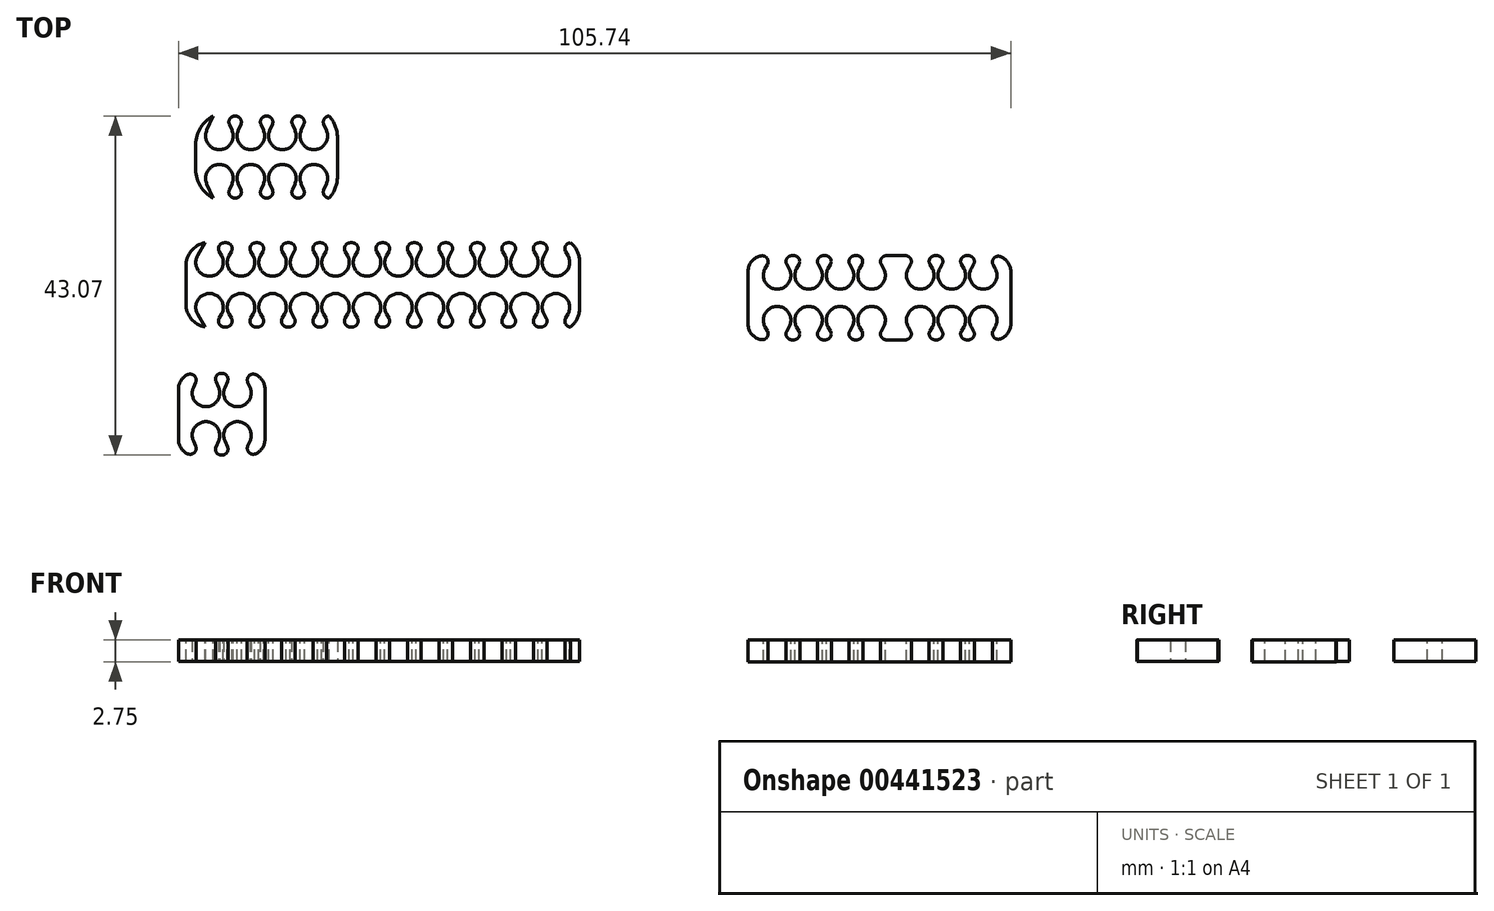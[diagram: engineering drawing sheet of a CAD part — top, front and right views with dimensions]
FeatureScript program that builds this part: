
annotation { "Feature Type Name" : "Feature", "Feature Type Description" : "" }
export const myFeature = defineFeature(function(context is Context, id is Id, definition is map)
    precondition{}
    {
        {
            var Q0;
            Q0=qCreatedBy(makeId("Top.planeOp"),FACE);
            var sketch = newSketch(context, id + "F0", { "sketchPlane" : qUnion([Q0])});
            skLineSegment(sketch, "E0.bottom", {"start": v(-25, 10.7) * mm, "end": v(25, 10.7) * mm});
            skLineSegment(sketch, "E0.top", {"start": v(-25, 0) * mm, "end": v(25, 0) * mm});
            skLineSegment(sketch, "E0.left", {"start": v(-25, 10.7) * mm, "end": v(-25, 0) * mm});
            skLineSegment(sketch, "E0.right", {"start": v(25, 10.7) * mm, "end": v(25, 0) * mm});
            skSolve(sketch);
        }
        {
            var Q0;
            Q0=makeQuery(id+"F0.imprint","IMPRINT",FACE,{"disambiguationData":[TD([[makeQuery(id+"F0.imprint","IMPRINT",EDGE,{"derivedFrom":sQuery(id+"F0.wireOp",EDGE,"E0.bottom")}),-1.0]])]});
            extrude(context, id + "F1", {"entities" : qUnion([Q0]), "depth" : 2.7 * mm});
        }
        {
            var Q0;
            Q0=makeQuery(id+"F1.opExtrude","CAP_FACE",FACE,{"disambiguationData":[OSD([sQuery(id+"F0.wireOp",EDGE,"E0.bottom"),sQuery(id+"F0.wireOp",EDGE,"E0.top"),sQuery(id+"F0.wireOp",EDGE,"E0.left"),sQuery(id+"F0.wireOp",EDGE,"E0.right")])],"isStart":false});
            var sketch = newSketch(context, id + "F2", { "sketchPlane" : qUnion([Q0])});
            skArc(sketch, "E1", {"start": v(-23.52, 9.07) * mm, "mid": v(-22, 6.45) * mm, "end": v(-20.48, 9.07) * mm});
            skArc(sketch, "E2", {"start": v(-19.52, 9.07) * mm, "mid": v(-18, 6.45) * mm, "end": v(-16.48, 9.07) * mm});
            skArc(sketch, "E3", {"start": v(-15.52, 9.07) * mm, "mid": v(-14, 6.45) * mm, "end": v(-12.48, 9.07) * mm});
            skArc(sketch, "E4", {"start": v(-11.52, 9.07) * mm, "mid": v(-10, 6.45) * mm, "end": v(-8.48, 9.07) * mm});
            skArc(sketch, "E5", {"start": v(-7.52, 9.07) * mm, "mid": v(-6, 6.45) * mm, "end": v(-4.48, 9.07) * mm});
            skArc(sketch, "E6", {"start": v(-3.52, 9.07) * mm, "mid": v(-2, 6.45) * mm, "end": v(-0.48, 9.07) * mm});
            skLineSegment(sketch, "E7", {"start": v(-19.52, 9.07) * mm, "end": v(-18.59, 10.7) * mm});
            skLineSegment(sketch, "E8", {"start": v(-16.48, 9.07) * mm, "end": v(-17.41, 10.7) * mm});
            skLineSegment(sketch, "E9", {"start": v(-15.52, 9.07) * mm, "end": v(-14.59, 10.7) * mm});
            skLineSegment(sketch, "E10", {"start": v(-12.48, 9.07) * mm, "end": v(-13.41, 10.7) * mm});
            skLineSegment(sketch, "E11", {"start": v(-11.52, 9.07) * mm, "end": v(-10.59, 10.7) * mm});
            skLineSegment(sketch, "E12", {"start": v(-8.48, 9.07) * mm, "end": v(-9.41, 10.7) * mm});
            skLineSegment(sketch, "E13", {"start": v(-7.52, 9.07) * mm, "end": v(-6.59, 10.7) * mm});
            skLineSegment(sketch, "E14", {"start": v(-4.48, 9.07) * mm, "end": v(-5.41, 10.7) * mm});
            skLineSegment(sketch, "E15", {"start": v(-0.48, 9.07) * mm, "end": v(-1.41, 10.7) * mm});
            skLineSegment(sketch, "E16", {"start": v(-23.52, 9.07) * mm, "end": v(-22.59, 10.7) * mm});
            skLineSegment(sketch, "E17", {"start": v(-18.59, 10.7) * mm, "end": v(-17.41, 10.7) * mm});
            skLineSegment(sketch, "E18", {"start": v(-14.59, 10.7) * mm, "end": v(-13.41, 10.7) * mm});
            skLineSegment(sketch, "E19", {"start": v(-10.59, 10.7) * mm, "end": v(-9.41, 10.7) * mm});
            skLineSegment(sketch, "E20", {"start": v(-6.59, 10.7) * mm, "end": v(-5.41, 10.7) * mm});
            skLineSegment(sketch, "E21", {"start": v(-2.59, 10.7) * mm, "end": v(-1.41, 10.7) * mm});
            skLineSegment(sketch, "E22", {"start": v(-25, 5.35) * mm, "end": v(25, 5.35) * mm});
            skLineSegment(sketch, "E23.MirrorCS", {"start": v(-15.52, 1.63) * mm, "end": v(-14.59, 0) * mm});
            skLineSegment(sketch, "E24.MirrorCS", {"start": v(-8.48, 1.63) * mm, "end": v(-9.41, 0) * mm});
            skLineSegment(sketch, "E25.MirrorCS", {"start": v(-7.52, 1.63) * mm, "end": v(-6.59, 0) * mm});
            skLineSegment(sketch, "E26.MirrorCS", {"start": v(-16.48, 1.63) * mm, "end": v(-17.41, 0) * mm});
            skLineSegment(sketch, "E27.MirrorCS", {"start": v(-4.48, 1.63) * mm, "end": v(-5.41, 0) * mm});
            skArc(sketch, "E28.MirrorCS", {"start": v(-23.52, 1.63) * mm, "mid": v(-22, 4.25) * mm, "end": v(-20.48, 1.63) * mm});
            skArc(sketch, "E29.MirrorCS", {"start": v(-3.52, 1.63) * mm, "mid": v(-2, 4.25) * mm, "end": v(-0.48, 1.63) * mm});
            skLineSegment(sketch, "E30.MirrorCS", {"start": v(-19.52, 1.63) * mm, "end": v(-18.59, 0) * mm});
            skArc(sketch, "E31.MirrorCS", {"start": v(-19.52, 1.63) * mm, "mid": v(-18, 4.25) * mm, "end": v(-16.48, 1.63) * mm});
            skArc(sketch, "E32.MirrorCS", {"start": v(-7.52, 1.63) * mm, "mid": v(-6, 4.25) * mm, "end": v(-4.48, 1.63) * mm});
            skArc(sketch, "E33.MirrorCS", {"start": v(-11.52, 1.63) * mm, "mid": v(-10, 4.25) * mm, "end": v(-8.48, 1.63) * mm});
            skArc(sketch, "E34.MirrorCS", {"start": v(-15.52, 1.63) * mm, "mid": v(-14, 4.25) * mm, "end": v(-12.48, 1.63) * mm});
            skLineSegment(sketch, "E35.MirrorCS", {"start": v(-23.52, 1.63) * mm, "end": v(-22.59, 0) * mm});
            skLineSegment(sketch, "E36.MirrorCS", {"start": v(-2.59, 0) * mm, "end": v(-1.41, 0) * mm});
            skLineSegment(sketch, "E37.MirrorCS", {"start": v(-6.59, 0) * mm, "end": v(-5.41, 0) * mm});
            skLineSegment(sketch, "E38.MirrorCS", {"start": v(-18.59, 0) * mm, "end": v(-17.41, 0) * mm});
            skLineSegment(sketch, "E39.MirrorCS", {"start": v(-11.52, 1.63) * mm, "end": v(-10.59, 0) * mm});
            skLineSegment(sketch, "E40.MirrorCS", {"start": v(-14.59, 0) * mm, "end": v(-13.41, 0) * mm});
            skLineSegment(sketch, "E41.MirrorCS", {"start": v(-10.59, 0) * mm, "end": v(-9.41, 0) * mm});
            skLineSegment(sketch, "E42.MirrorCS", {"start": v(-12.48, 1.63) * mm, "end": v(-13.41, 0) * mm});
            skLineSegment(sketch, "E43.MirrorCS", {"start": v(-0.48, 1.63) * mm, "end": v(-1.41, 0) * mm});
            skLineSegment(sketch, "E44", {"start": v(-3.52, 9.07) * mm, "end": v(-2.59, 10.7) * mm});
            skLineSegment(sketch, "E45", {"start": v(-3.52, 1.63) * mm, "end": v(-2.59, 0) * mm});
            skLineSegment(sketch, "E46", {"start": v(-20.48, 9.07) * mm, "end": v(-21.41, 10.7) * mm});
            skLineSegment(sketch, "E47", {"start": v(-21.41, 10.7) * mm, "end": v(-22.59, 10.7) * mm});
            skLineSegment(sketch, "E48", {"start": v(-20.48, 1.63) * mm, "end": v(-21.41, 0) * mm});
            skLineSegment(sketch, "E49", {"start": v(-21.41, 0) * mm, "end": v(-22.59, 0) * mm});
            skLineSegment(sketch, "E50.MirrorCS", {"start": v(6.59, 0) * mm, "end": v(5.41, 0) * mm});
            skLineSegment(sketch, "E51.MirrorCS", {"start": v(21.41, 0) * mm, "end": v(22.59, 0) * mm});
            skLineSegment(sketch, "E52.MirrorCS", {"start": v(10.59, 10.7) * mm, "end": v(9.41, 10.7) * mm});
            skLineSegment(sketch, "E53.MirrorCS", {"start": v(6.59, 10.7) * mm, "end": v(5.41, 10.7) * mm});
            skLineSegment(sketch, "E54.MirrorCS", {"start": v(21.41, 10.7) * mm, "end": v(22.59, 10.7) * mm});
            skLineSegment(sketch, "E55.MirrorCS", {"start": v(18.59, 10.7) * mm, "end": v(17.41, 10.7) * mm});
            skLineSegment(sketch, "E56.MirrorCS", {"start": v(2.59, 0) * mm, "end": v(1.41, 0) * mm});
            skLineSegment(sketch, "E57.MirrorCS", {"start": v(18.59, 0) * mm, "end": v(17.41, 0) * mm});
            skLineSegment(sketch, "E58.MirrorCS", {"start": v(2.59, 10.7) * mm, "end": v(1.41, 10.7) * mm});
            skLineSegment(sketch, "E59.MirrorCS", {"start": v(10.59, 0) * mm, "end": v(9.41, 0) * mm});
            skLineSegment(sketch, "E60.MirrorCS", {"start": v(14.59, 10.7) * mm, "end": v(13.41, 10.7) * mm});
            skLineSegment(sketch, "E61.MirrorCS", {"start": v(14.59, 0) * mm, "end": v(13.41, 0) * mm});
            skArc(sketch, "E62.MirrorCS", {"start": v(11.52, 9.07) * mm, "mid": v(10, 6.45) * mm, "end": v(8.48, 9.07) * mm});
            skLineSegment(sketch, "E63.MirrorCS", {"start": v(15.52, 1.63) * mm, "end": v(14.59, 0) * mm});
            skArc(sketch, "E64.MirrorCS", {"start": v(15.52, 1.63) * mm, "mid": v(14, 4.25) * mm, "end": v(12.48, 1.63) * mm});
            skLineSegment(sketch, "E65.MirrorCS", {"start": v(4.48, 1.63) * mm, "end": v(5.41, 0) * mm});
            skArc(sketch, "E66.MirrorCS", {"start": v(3.52, 1.63) * mm, "mid": v(2, 4.25) * mm, "end": v(0.48, 1.63) * mm});
            skArc(sketch, "E67.MirrorCS", {"start": v(3.52, 9.07) * mm, "mid": v(2, 6.45) * mm, "end": v(0.48, 9.07) * mm});
            skLineSegment(sketch, "E68.MirrorCS", {"start": v(15.52, 9.07) * mm, "end": v(14.59, 10.7) * mm});
            skLineSegment(sketch, "E69.MirrorCS", {"start": v(12.48, 9.07) * mm, "end": v(13.41, 10.7) * mm});
            skLineSegment(sketch, "E70.MirrorCS", {"start": v(16.48, 9.07) * mm, "end": v(17.41, 10.7) * mm});
            skLineSegment(sketch, "E71.MirrorCS", {"start": v(23.52, 9.07) * mm, "end": v(22.59, 10.7) * mm});
            skArc(sketch, "E72.MirrorCS", {"start": v(7.52, 9.07) * mm, "mid": v(6, 6.45) * mm, "end": v(4.48, 9.07) * mm});
            skLineSegment(sketch, "E73.MirrorCS", {"start": v(25, 5.35) * mm, "end": v(-25, 5.35) * mm});
            skLineSegment(sketch, "E74.MirrorCS", {"start": v(7.52, 1.63) * mm, "end": v(6.59, 0) * mm});
            skArc(sketch, "E75.MirrorCS", {"start": v(19.52, 9.07) * mm, "mid": v(18, 6.45) * mm, "end": v(16.48, 9.07) * mm});
            skLineSegment(sketch, "E76.MirrorCS", {"start": v(3.52, 1.63) * mm, "end": v(2.59, 0) * mm});
            skLineSegment(sketch, "E77.MirrorCS", {"start": v(19.52, 1.63) * mm, "end": v(18.59, 0) * mm});
            skLineSegment(sketch, "E78.MirrorCS", {"start": v(23.52, 1.63) * mm, "end": v(22.59, 0) * mm});
            skArc(sketch, "E79.MirrorCS", {"start": v(15.52, 9.07) * mm, "mid": v(14, 6.45) * mm, "end": v(12.48, 9.07) * mm});
            skArc(sketch, "E80.MirrorCS", {"start": v(11.52, 1.63) * mm, "mid": v(10, 4.25) * mm, "end": v(8.48, 1.63) * mm});
            skArc(sketch, "E81.MirrorCS", {"start": v(7.52, 1.63) * mm, "mid": v(6, 4.25) * mm, "end": v(4.48, 1.63) * mm});
            skLineSegment(sketch, "E82.MirrorCS", {"start": v(12.48, 1.63) * mm, "end": v(13.41, 0) * mm});
            skLineSegment(sketch, "E83.MirrorCS", {"start": v(8.48, 9.07) * mm, "end": v(9.41, 10.7) * mm});
            skArc(sketch, "E84.MirrorCS", {"start": v(23.52, 9.07) * mm, "mid": v(22, 6.45) * mm, "end": v(20.48, 9.07) * mm});
            skLineSegment(sketch, "E85.MirrorCS", {"start": v(20.48, 9.07) * mm, "end": v(21.41, 10.7) * mm});
            skLineSegment(sketch, "E86.MirrorCS", {"start": v(7.52, 9.07) * mm, "end": v(6.59, 10.7) * mm});
            skLineSegment(sketch, "E87.MirrorCS", {"start": v(0.48, 1.63) * mm, "end": v(1.41, 0) * mm});
            skLineSegment(sketch, "E88.MirrorCS", {"start": v(16.48, 1.63) * mm, "end": v(17.41, 0) * mm});
            skLineSegment(sketch, "E89.MirrorCS", {"start": v(20.48, 1.63) * mm, "end": v(21.41, 0) * mm});
            skLineSegment(sketch, "E90.MirrorCS", {"start": v(11.52, 1.63) * mm, "end": v(10.59, 0) * mm});
            skLineSegment(sketch, "E91.MirrorCS", {"start": v(11.52, 9.07) * mm, "end": v(10.59, 10.7) * mm});
            skArc(sketch, "E92.MirrorCS", {"start": v(23.52, 1.63) * mm, "mid": v(22, 4.25) * mm, "end": v(20.48, 1.63) * mm});
            skLineSegment(sketch, "E93.MirrorCS", {"start": v(3.52, 9.07) * mm, "end": v(2.59, 10.7) * mm});
            skArc(sketch, "E94.MirrorCS", {"start": v(19.52, 1.63) * mm, "mid": v(18, 4.25) * mm, "end": v(16.48, 1.63) * mm});
            skLineSegment(sketch, "E95.MirrorCS", {"start": v(4.48, 9.07) * mm, "end": v(5.41, 10.7) * mm});
            skLineSegment(sketch, "E96.MirrorCS", {"start": v(19.52, 9.07) * mm, "end": v(18.59, 10.7) * mm});
            skLineSegment(sketch, "E97.MirrorCS", {"start": v(8.48, 1.63) * mm, "end": v(9.41, 0) * mm});
            skLineSegment(sketch, "E98.MirrorCS", {"start": v(0.48, 9.07) * mm, "end": v(1.41, 10.7) * mm});
            skArc(sketch, "E99", {"start": v(48.58, 7.43) * mm, "mid": v(50.1, 4.82) * mm, "end": v(51.62, 7.43) * mm});
            skLineSegment(sketch, "E100", {"start": v(51.62, 7.43) * mm, "end": v(50.69, 9.07) * mm});
            skArc(sketch, "E101.MirrorCS", {"start": v(48.58, 0) * mm, "mid": v(50.1, 2.62) * mm, "end": v(51.62, 0) * mm});
            skLineSegment(sketch, "E102.MirrorCS", {"start": v(51.62, 0) * mm, "end": v(50.69, -1.63) * mm});
            skLineSegment(sketch, "E103", {"start": v(48.58, 7.43) * mm, "end": v(49.51, 9.07) * mm});
            skLineSegment(sketch, "E104", {"start": v(48.58, 0) * mm, "end": v(49.51, -1.63) * mm});
            skArc(sketch, "E105.MirrorCS", {"start": v(63.62, 7.43) * mm, "mid": v(62.1, 4.82) * mm, "end": v(60.58, 7.43) * mm});
            skLineSegment(sketch, "E106.MirrorCS", {"start": v(56.58, 0) * mm, "end": v(57.51, -1.63) * mm});
            skArc(sketch, "E107.MirrorCS", {"start": v(55.62, 0) * mm, "mid": v(54.1, 2.62) * mm, "end": v(52.58, 0) * mm});
            skArc(sketch, "E108.MirrorCS", {"start": v(55.62, 7.43) * mm, "mid": v(54.1, 4.82) * mm, "end": v(52.58, 7.43) * mm});
            skArc(sketch, "E109.MirrorCS", {"start": v(59.62, 7.43) * mm, "mid": v(58.1, 4.82) * mm, "end": v(56.58, 7.43) * mm});
            skLineSegment(sketch, "E110.MirrorCS", {"start": v(59.62, 0) * mm, "end": v(58.69, -1.63) * mm});
            skLineSegment(sketch, "E111.MirrorCS", {"start": v(55.62, 0) * mm, "end": v(54.69, -1.63) * mm});
            skArc(sketch, "E112.MirrorCS", {"start": v(63.62, 0) * mm, "mid": v(62.1, 2.62) * mm, "end": v(60.58, 0) * mm});
            skArc(sketch, "E113.MirrorCS", {"start": v(59.62, 0) * mm, "mid": v(58.1, 2.62) * mm, "end": v(56.58, 0) * mm});
            skLineSegment(sketch, "E114.MirrorCS", {"start": v(60.58, 7.43) * mm, "end": v(61.51, 9.07) * mm});
            skLineSegment(sketch, "E115.MirrorCS", {"start": v(59.62, 7.43) * mm, "end": v(58.69, 9.07) * mm});
            skLineSegment(sketch, "E116.MirrorCS", {"start": v(52.58, 0) * mm, "end": v(53.51, -1.63) * mm});
            skLineSegment(sketch, "E117.MirrorCS", {"start": v(63.62, 0) * mm, "end": v(62.69, -1.63) * mm});
            skLineSegment(sketch, "E118.MirrorCS", {"start": v(63.62, 7.43) * mm, "end": v(62.69, 9.07) * mm});
            skLineSegment(sketch, "E119.MirrorCS", {"start": v(55.62, 7.43) * mm, "end": v(54.69, 9.07) * mm});
            skLineSegment(sketch, "E120.MirrorCS", {"start": v(56.58, 7.43) * mm, "end": v(57.51, 9.07) * mm});
            skLineSegment(sketch, "E121.MirrorCS", {"start": v(60.58, 0) * mm, "end": v(61.51, -1.63) * mm});
            skLineSegment(sketch, "E122.MirrorCS", {"start": v(52.58, 7.43) * mm, "end": v(53.51, 9.07) * mm});
            skPoint(sketch, "E123.firstSnap0", {"position": v(50.1, 9.07) * mm});
            skLineSegment(sketch, "E123.bottom", {"start": v(46.4, 9.07) * mm, "end": v(49.51, 9.07) * mm});
            skLineSegment(sketch, "E123.top", {"start": v(46.4, -1.63) * mm, "end": v(49.51, -1.63) * mm});
            skLineSegment(sketch, "E123.left", {"start": v(46.4, 9.07) * mm, "end": v(46.4, -1.63) * mm});
            skLineSegment(sketch, "E124.trimOffspring", {"start": v(50.69, -1.63) * mm, "end": v(53.51, -1.63) * mm});
            skLineSegment(sketch, "E125.trimOffspring", {"start": v(54.69, -1.63) * mm, "end": v(57.51, -1.63) * mm});
            skLineSegment(sketch, "E126.trimOffspring", {"start": v(58.69, -1.63) * mm, "end": v(61.51, -1.63) * mm});
            skLineSegment(sketch, "E127.trimOffspring", {"start": v(58.69, 9.07) * mm, "end": v(61.51, 9.07) * mm});
            skLineSegment(sketch, "E128.trimOffspring", {"start": v(54.69, 9.07) * mm, "end": v(57.51, 9.07) * mm});
            skLineSegment(sketch, "E129.trimOffspring", {"start": v(50.69, 9.07) * mm, "end": v(53.51, 9.07) * mm});
            skLineSegment(sketch, "E130", {"start": v(62.69, 9.07) * mm, "end": v(65.32, 9.07) * mm});
            skLineSegment(sketch, "E131", {"start": v(62.69, -1.63) * mm, "end": v(65.32, -1.63) * mm});
            skLineSegment(sketch, "E132.MirrorCS", {"start": v(75.69, 9.07) * mm, "end": v(72.87, 9.07) * mm});
            skLineSegment(sketch, "E133.MirrorCS", {"start": v(69.8, 7.43) * mm, "end": v(68.87, 9.07) * mm});
            skLineSegment(sketch, "E134.MirrorCS", {"start": v(70.76, 0) * mm, "end": v(71.69, -1.63) * mm});
            skLineSegment(sketch, "E135.MirrorCS", {"start": v(70.76, 7.43) * mm, "end": v(71.69, 9.07) * mm});
            skLineSegment(sketch, "E136.MirrorCS", {"start": v(75.69, -1.63) * mm, "end": v(72.87, -1.63) * mm});
            skLineSegment(sketch, "E137.MirrorCS", {"start": v(71.69, 9.07) * mm, "end": v(68.87, 9.07) * mm});
            skArc(sketch, "E138.MirrorCS", {"start": v(66.76, 0) * mm, "mid": v(68.28, 2.62) * mm, "end": v(69.8, 0) * mm});
            skArc(sketch, "E139.MirrorCS", {"start": v(70.76, 0) * mm, "mid": v(72.28, 2.62) * mm, "end": v(73.8, 0) * mm});
            skArc(sketch, "E140.MirrorCS", {"start": v(74.76, 7.43) * mm, "mid": v(76.28, 4.82) * mm, "end": v(77.8, 7.43) * mm});
            skArc(sketch, "E141.MirrorCS", {"start": v(70.76, 7.43) * mm, "mid": v(72.28, 4.82) * mm, "end": v(73.8, 7.43) * mm});
            skLineSegment(sketch, "E142.MirrorCS", {"start": v(77.8, 7.43) * mm, "end": v(76.87, 9.07) * mm});
            skLineSegment(sketch, "E143.MirrorCS", {"start": v(73.8, 0) * mm, "end": v(72.87, -1.63) * mm});
            skLineSegment(sketch, "E144.MirrorCS", {"start": v(69.8, 0) * mm, "end": v(68.87, -1.63) * mm});
            skLineSegment(sketch, "E145.MirrorCS", {"start": v(66.76, 7.43) * mm, "end": v(67.69, 9.07) * mm});
            skLineSegment(sketch, "E146.MirrorCS", {"start": v(71.69, -1.63) * mm, "end": v(68.87, -1.63) * mm});
            skLineSegment(sketch, "E147.MirrorCS", {"start": v(77.8, 0) * mm, "end": v(76.87, -1.63) * mm});
            skArc(sketch, "E148.MirrorCS", {"start": v(74.76, 0) * mm, "mid": v(76.28, 2.62) * mm, "end": v(77.8, 0) * mm});
            skArc(sketch, "E149.MirrorCS", {"start": v(66.76, 7.43) * mm, "mid": v(68.28, 4.82) * mm, "end": v(69.8, 7.43) * mm});
            skLineSegment(sketch, "E150.MirrorCS", {"start": v(73.8, 7.43) * mm, "end": v(72.87, 9.07) * mm});
            skLineSegment(sketch, "E151.MirrorCS", {"start": v(74.76, 7.43) * mm, "end": v(75.69, 9.07) * mm});
            skLineSegment(sketch, "E152.MirrorCS", {"start": v(66.76, 0) * mm, "end": v(67.69, -1.63) * mm});
            skLineSegment(sketch, "E153.MirrorCS", {"start": v(74.76, 0) * mm, "end": v(75.69, -1.63) * mm});
            skLineSegment(sketch, "E154", {"start": v(65.32, 9.07) * mm, "end": v(67.69, 9.07) * mm});
            skLineSegment(sketch, "E155", {"start": v(65.32, -1.63) * mm, "end": v(67.69, -1.63) * mm});
            skLineSegment(sketch, "E156", {"start": v(79.78, 9.07) * mm, "end": v(79.78, -1.63) * mm});
            skLineSegment(sketch, "E157", {"start": v(79.78, -1.63) * mm, "end": v(76.87, -1.63) * mm});
            skLineSegment(sketch, "E158", {"start": v(76.87, 9.07) * mm, "end": v(79.78, 9.07) * mm});
            skSolve(sketch);
        }
        {
            var Q0;
            Q0 = qSketchRegion(id + "F2", true);
            extrude(context, id + "F3", {"entities" : qUnion([Q0]), "operationType" : NewBodyOperationType.REMOVE, "oppositeDirection" : true, "depth" : 25 * mm});
        }
        {
            var Q0;
            Q0=makeQuery(id+"F3.boolean.opBoolean","COPY",EDGE,{"derivedFrom":makeQuery(id+"F3.opExtrude","SWEPT_EDGE",EDGE,{"disambiguationData":[OSD([sQuery(id+"F0.wireOp",EDGE,"E0.top"),sQuery(id+"F2.wireOp",EDGE,"E244.MirrorCS"),sQuery(id+"F2.wireOp",EDGE,"E248.MirrorCS")])]})});
            var Q1;
            Q1=makeQuery(id+"F3.boolean.opBoolean","COPY",EDGE,{"derivedFrom":makeQuery(id+"F3.opExtrude","SWEPT_EDGE",EDGE,{"disambiguationData":[OSD([sQuery(id+"F0.wireOp",EDGE,"E0.top"),sQuery(id+"F2.wireOp",EDGE,"E247.MirrorCS"),sQuery(id+"F2.wireOp",EDGE,"E248.MirrorCS")])]})});
            var Q2;
            Q2=makeQuery(id+"F3.boolean.opBoolean","COPY",EDGE,{"derivedFrom":makeQuery(id+"F3.opExtrude","SWEPT_EDGE",EDGE,{"disambiguationData":[OSD([sQuery(id+"F0.wireOp",EDGE,"E0.bottom"),sQuery(id+"F2.wireOp",EDGE,"IQOr8gKH-AA3r-RsNy-xa8J-JxTkXKXGDwke"),sQuery(id+"F2.wireOp",EDGE,"qSGI12MA-lLNW-cEYR-Ucfo-gfGJAkbjLQMW")])]})});
            var Q3;
            Q3=makeQuery(id+"F3.boolean.opBoolean","COPY",EDGE,{"derivedFrom":makeQuery(id+"F3.opExtrude","SWEPT_EDGE",EDGE,{"disambiguationData":[OSD([sQuery(id+"F0.wireOp",EDGE,"E0.top"),sQuery(id+"F2.wireOp",EDGE,"E36.MirrorCS"),sQuery(id+"F2.wireOp",EDGE,"E43.MirrorCS")])]})});
            var Q4;
            Q4=makeQuery(id+"F3.boolean.opBoolean","COPY",EDGE,{"derivedFrom":makeQuery(id+"F3.opExtrude","SWEPT_EDGE",EDGE,{"disambiguationData":[OSD([sQuery(id+"F0.wireOp",EDGE,"E0.top"),sQuery(id+"F2.wireOp",EDGE,"E243.MirrorCS"),sQuery(id+"F2.wireOp",EDGE,"E36.MirrorCS")])]})});
            var Q5;
            Q5=makeQuery(id+"F3.boolean.opBoolean","COPY",EDGE,{"derivedFrom":makeQuery(id+"F3.opExtrude","SWEPT_EDGE",EDGE,{"disambiguationData":[OSD([sQuery(id+"F0.wireOp",EDGE,"E0.top"),sQuery(id+"F2.wireOp",EDGE,"E27.MirrorCS"),sQuery(id+"F2.wireOp",EDGE,"E37.MirrorCS")])]})});
            var Q6;
            Q6=makeQuery(id+"F3.boolean.opBoolean","COPY",EDGE,{"derivedFrom":makeQuery(id+"F3.opExtrude","SWEPT_EDGE",EDGE,{"disambiguationData":[OSD([sQuery(id+"F0.wireOp",EDGE,"E0.top"),sQuery(id+"F2.wireOp",EDGE,"E25.MirrorCS"),sQuery(id+"F2.wireOp",EDGE,"E37.MirrorCS")])]})});
            var Q7;
            Q7=makeQuery(id+"F3.boolean.opBoolean","COPY",EDGE,{"derivedFrom":makeQuery(id+"F3.opExtrude","SWEPT_EDGE",EDGE,{"disambiguationData":[OSD([sQuery(id+"F0.wireOp",EDGE,"E0.top"),sQuery(id+"F2.wireOp",EDGE,"E24.MirrorCS"),sQuery(id+"F2.wireOp",EDGE,"E41.MirrorCS")])]})});
            var Q8;
            Q8=makeQuery(id+"F3.boolean.opBoolean","COPY",EDGE,{"derivedFrom":makeQuery(id+"F3.opExtrude","SWEPT_EDGE",EDGE,{"disambiguationData":[OSD([sQuery(id+"F0.wireOp",EDGE,"E0.top"),sQuery(id+"F2.wireOp",EDGE,"E39.MirrorCS"),sQuery(id+"F2.wireOp",EDGE,"E41.MirrorCS")])]})});
            var Q9;
            Q9=makeQuery(id+"F3.boolean.opBoolean","COPY",EDGE,{"derivedFrom":makeQuery(id+"F3.opExtrude","SWEPT_EDGE",EDGE,{"disambiguationData":[OSD([sQuery(id+"F0.wireOp",EDGE,"E0.top"),sQuery(id+"F2.wireOp",EDGE,"E40.MirrorCS"),sQuery(id+"F2.wireOp",EDGE,"E42.MirrorCS")])]})});
            var Q10;
            Q10=makeQuery(id+"F3.boolean.opBoolean","COPY",EDGE,{"derivedFrom":makeQuery(id+"F3.opExtrude","SWEPT_EDGE",EDGE,{"disambiguationData":[OSD([sQuery(id+"F0.wireOp",EDGE,"E0.top"),sQuery(id+"F2.wireOp",EDGE,"E23.MirrorCS"),sQuery(id+"F2.wireOp",EDGE,"E40.MirrorCS")])]})});
            var Q11;
            Q11=makeQuery(id+"F3.boolean.opBoolean","COPY",EDGE,{"derivedFrom":makeQuery(id+"F3.opExtrude","SWEPT_EDGE",EDGE,{"disambiguationData":[OSD([sQuery(id+"F0.wireOp",EDGE,"E0.top"),sQuery(id+"F2.wireOp",EDGE,"E26.MirrorCS"),sQuery(id+"F2.wireOp",EDGE,"E38.MirrorCS")])]})});
            var Q12;
            Q12=makeQuery(id+"F3.boolean.opBoolean","COPY",EDGE,{"derivedFrom":makeQuery(id+"F3.opExtrude","SWEPT_EDGE",EDGE,{"disambiguationData":[OSD([sQuery(id+"F0.wireOp",EDGE,"E0.top"),sQuery(id+"F2.wireOp",EDGE,"E30.MirrorCS"),sQuery(id+"F2.wireOp",EDGE,"E38.MirrorCS")])]})});
            var Q13;
            Q13=makeQuery(id+"F3.boolean.opBoolean","COPY",EDGE,{"derivedFrom":makeQuery(id+"F3.opExtrude","SWEPT_EDGE",EDGE,{"disambiguationData":[OSD([sQuery(id+"F0.wireOp",EDGE,"E0.top"),sQuery(id+"F2.wireOp",EDGE,"E254.MirrorCS"),sQuery(id+"F2.wireOp",EDGE,"E255.MirrorCS")])]})});
            var Q14;
            Q14=makeQuery(id+"F3.boolean.opBoolean","COPY",EDGE,{"derivedFrom":makeQuery(id+"F3.opExtrude","SWEPT_EDGE",EDGE,{"disambiguationData":[OSD([sQuery(id+"F0.wireOp",EDGE,"E0.top"),sQuery(id+"F2.wireOp",EDGE,"E35.MirrorCS"),sQuery(id+"F2.wireOp",EDGE,"E254.MirrorCS")])]})});
            var Q15;
            Q15=makeQuery(id+"F3.boolean.opBoolean","COPY",EDGE,{"derivedFrom":makeQuery(id+"F3.opExtrude","SWEPT_EDGE",EDGE,{"disambiguationData":[OSD([sQuery(id+"F0.wireOp",EDGE,"E0.bottom"),sQuery(id+"F2.wireOp",EDGE,"UjLKNyOy-sdcN-vUJI-xe36-BtCcAArnIZbs"),sQuery(id+"F2.wireOp",EDGE,"qSGI12MA-lLNW-cEYR-Ucfo-gfGJAkbjLQMW")])]})});
            var Q16;
            Q16=makeQuery(id+"F3.boolean.opBoolean","COPY",EDGE,{"derivedFrom":makeQuery(id+"F3.opExtrude","SWEPT_EDGE",EDGE,{"disambiguationData":[OSD([sQuery(id+"F0.wireOp",EDGE,"E0.bottom"),sQuery(id+"F2.wireOp",EDGE,"E15"),sQuery(id+"F2.wireOp",EDGE,"E21")])]})});
            var Q17;
            Q17=makeQuery(id+"F3.boolean.opBoolean","COPY",EDGE,{"derivedFrom":makeQuery(id+"F3.opExtrude","SWEPT_EDGE",EDGE,{"disambiguationData":[OSD([sQuery(id+"F0.wireOp",EDGE,"E0.bottom"),sQuery(id+"F2.wireOp",EDGE,"1lPn1qKL-qkZ3-ByxJ-MAWl-Qf6jtQHj3nnD"),sQuery(id+"F2.wireOp",EDGE,"E21")])]})});
            var Q18;
            Q18=makeQuery(id+"F3.boolean.opBoolean","COPY",EDGE,{"derivedFrom":makeQuery(id+"F3.opExtrude","SWEPT_EDGE",EDGE,{"disambiguationData":[OSD([sQuery(id+"F0.wireOp",EDGE,"E0.bottom"),sQuery(id+"F2.wireOp",EDGE,"E14"),sQuery(id+"F2.wireOp",EDGE,"E20")])]})});
            var Q19;
            Q19=makeQuery(id+"F3.boolean.opBoolean","COPY",EDGE,{"derivedFrom":makeQuery(id+"F3.opExtrude","SWEPT_EDGE",EDGE,{"disambiguationData":[OSD([sQuery(id+"F0.wireOp",EDGE,"E0.bottom"),sQuery(id+"F2.wireOp",EDGE,"E13"),sQuery(id+"F2.wireOp",EDGE,"E20")])]})});
            var Q20;
            Q20=makeQuery(id+"F3.boolean.opBoolean","COPY",EDGE,{"derivedFrom":makeQuery(id+"F3.opExtrude","SWEPT_EDGE",EDGE,{"disambiguationData":[OSD([sQuery(id+"F0.wireOp",EDGE,"E0.bottom"),sQuery(id+"F2.wireOp",EDGE,"E12"),sQuery(id+"F2.wireOp",EDGE,"E19")])]})});
            var Q21;
            Q21=makeQuery(id+"F3.boolean.opBoolean","COPY",EDGE,{"derivedFrom":makeQuery(id+"F3.opExtrude","SWEPT_EDGE",EDGE,{"disambiguationData":[OSD([sQuery(id+"F0.wireOp",EDGE,"E0.bottom"),sQuery(id+"F2.wireOp",EDGE,"E10"),sQuery(id+"F2.wireOp",EDGE,"E18")])]})});
            var Q22;
            Q22=makeQuery(id+"F3.boolean.opBoolean","COPY",EDGE,{"derivedFrom":makeQuery(id+"F3.opExtrude","SWEPT_EDGE",EDGE,{"disambiguationData":[OSD([sQuery(id+"F0.wireOp",EDGE,"E0.bottom"),sQuery(id+"F2.wireOp",EDGE,"E9"),sQuery(id+"F2.wireOp",EDGE,"E18")])]})});
            var Q23;
            Q23=makeQuery(id+"F3.boolean.opBoolean","COPY",EDGE,{"derivedFrom":makeQuery(id+"F3.opExtrude","SWEPT_EDGE",EDGE,{"disambiguationData":[OSD([sQuery(id+"F0.wireOp",EDGE,"E0.bottom"),sQuery(id+"F2.wireOp",EDGE,"E8"),sQuery(id+"F2.wireOp",EDGE,"E17")])]})});
            var Q24;
            Q24=makeQuery(id+"F3.boolean.opBoolean","COPY",EDGE,{"derivedFrom":makeQuery(id+"F3.opExtrude","SWEPT_EDGE",EDGE,{"disambiguationData":[OSD([sQuery(id+"F0.wireOp",EDGE,"E0.bottom"),sQuery(id+"F2.wireOp",EDGE,"E7"),sQuery(id+"F2.wireOp",EDGE,"E17")])]})});
            var Q25;
            Q25=makeQuery(id+"F3.boolean.opBoolean","COPY",EDGE,{"derivedFrom":makeQuery(id+"F3.opExtrude","SWEPT_EDGE",EDGE,{"disambiguationData":[OSD([sQuery(id+"F0.wireOp",EDGE,"E0.bottom"),sQuery(id+"F2.wireOp",EDGE,"b1TfKxvo-d6YO-5rsT-L5gf-Kxo1XV25pjbY"),sQuery(id+"F2.wireOp",EDGE,"8bgCysRb-rjLR-dHsJ-Bppl-TsGBnFBbDExs")])]})});
            var Q26;
            Q26=makeQuery(id+"F3.boolean.opBoolean","COPY",EDGE,{"derivedFrom":makeQuery(id+"F3.opExtrude","SWEPT_EDGE",EDGE,{"disambiguationData":[OSD([sQuery(id+"F0.wireOp",EDGE,"E0.bottom"),sQuery(id+"F2.wireOp",EDGE,"E16"),sQuery(id+"F2.wireOp",EDGE,"8bgCysRb-rjLR-dHsJ-Bppl-TsGBnFBbDExs")])]})});
            var Q27;
            Q27=makeQuery(id+"F3.boolean.opBoolean","COPY",EDGE,{"derivedFrom":makeQuery(id+"F3.opExtrude","SWEPT_EDGE",EDGE,{"disambiguationData":[OSD([sQuery(id+"F0.wireOp",EDGE,"E0.bottom"),sQuery(id+"F2.wireOp",EDGE,"E11"),sQuery(id+"F2.wireOp",EDGE,"E19")])]})});
            fillet(context, id + "F4", {"entities" : qUnion([Q0, Q1, Q2, Q3, Q4, Q5, Q6, Q7, Q8, Q9, Q10, Q11, Q12, Q13, Q14, Q15, Q16, Q17, Q18, Q19, Q20, Q21, Q22, Q23, Q24, Q25, Q26, Q27]), "radius" : .75 * mm, "tangentPropagation" : true, "allowEdgeOverflow" : false});
        }
        {
            var Q0;
            Q0=makeQuery(id+"F1.opExtrude","SWEPT_EDGE",EDGE,{"disambiguationData":[OSD([sQuery(id+"F0.wireOp",EDGE,"E0.bottom"),sQuery(id+"F0.wireOp",EDGE,"E0.left")])]});
            var Q1;
            Q1=makeQuery(id+"F1.opExtrude","SWEPT_EDGE",EDGE,{"disambiguationData":[OSD([sQuery(id+"F0.wireOp",EDGE,"E0.top"),sQuery(id+"F0.wireOp",EDGE,"E0.left")])]});
            var Q2;
            Q2=makeQuery(id+"F1.opExtrude","SWEPT_EDGE",EDGE,{"disambiguationData":[OSD([sQuery(id+"F0.wireOp",EDGE,"E0.top"),sQuery(id+"F0.wireOp",EDGE,"E0.right")])]});
            var Q3;
            Q3=makeQuery(id+"F1.opExtrude","SWEPT_EDGE",EDGE,{"disambiguationData":[OSD([sQuery(id+"F0.wireOp",EDGE,"E0.bottom"),sQuery(id+"F0.wireOp",EDGE,"E0.right")])]});
            fillet(context, id + "F5", {"entities" : qUnion([Q0, Q1, Q2, Q3]), "radius" : 3 * mm, "tangentPropagation" : true, "allowEdgeOverflow" : false});
        }
        {
            var Q0;
            Q0=qCreatedBy(makeId("Top.planeOp"),FACE);
            var sketch = newSketch(context, id + "F6", { "sketchPlane" : qUnion([Q0])});
            skLineSegment(sketch, "E159.bottom", {"start": v(-23.75, 26.79) * mm, "end": v(-5.75, 26.79) * mm});
            skLineSegment(sketch, "E159.top", {"start": v(-23.75, 16.39) * mm, "end": v(-5.75, 16.39) * mm});
            skLineSegment(sketch, "E159.left", {"start": v(-23.75, 26.79) * mm, "end": v(-23.75, 16.39) * mm});
            skLineSegment(sketch, "E159.right", {"start": v(-5.75, 26.79) * mm, "end": v(-5.75, 16.39) * mm});
            skSolve(sketch);
        }
        {
            var Q0;
            Q0 = qSketchRegion(id + "F6", true);
            extrude(context, id + "F7", {"entities" : qUnion([Q0]), "depth" : 2.7 * mm});
        }
        {
            var Q0;
            Q0=makeQuery(id+"F7.opExtrude","CAP_FACE",FACE,{"disambiguationData":[OSD([sQuery(id+"F6.wireOp",EDGE,"E159.bottom"),sQuery(id+"F6.wireOp",EDGE,"E159.top"),sQuery(id+"F6.wireOp",EDGE,"E159.left"),sQuery(id+"F6.wireOp",EDGE,"E159.right")])],"isStart":false});
            var sketch = newSketch(context, id + "F8", { "sketchPlane" : qUnion([Q0])});
            skArc(sketch, "E160", {"start": v(-22.35, 25) * mm, "mid": v(-20.75, 22.54) * mm, "end": v(-19.16, 25) * mm});
            skArc(sketch, "E161", {"start": v(-18.35, 25) * mm, "mid": v(-16.75, 22.54) * mm, "end": v(-15.16, 25) * mm});
            skArc(sketch, "E162", {"start": v(-14.35, 25) * mm, "mid": v(-12.75, 22.54) * mm, "end": v(-11.16, 25) * mm});
            skArc(sketch, "E163", {"start": v(-10.35, 25) * mm, "mid": v(-8.75, 22.54) * mm, "end": v(-7.16, 25) * mm});
            skLineSegment(sketch, "E164", {"start": v(-22.35, 25) * mm, "end": v(-21.54, 26.79) * mm});
            skLineSegment(sketch, "E165", {"start": v(-19.16, 25) * mm, "end": v(-19.96, 26.79) * mm});
            skLineSegment(sketch, "E166", {"start": v(-19.96, 26.79) * mm, "end": v(-21.54, 26.79) * mm});
            skLineSegment(sketch, "E167", {"start": v(-18.35, 25) * mm, "end": v(-17.54, 26.79) * mm});
            skLineSegment(sketch, "E168", {"start": v(-15.16, 25) * mm, "end": v(-15.96, 26.79) * mm});
            skLineSegment(sketch, "E169", {"start": v(-15.96, 26.79) * mm, "end": v(-17.54, 26.79) * mm});
            skLineSegment(sketch, "E170", {"start": v(-14.35, 25) * mm, "end": v(-13.54, 26.79) * mm});
            skLineSegment(sketch, "E171", {"start": v(-11.16, 25) * mm, "end": v(-11.96, 26.79) * mm});
            skLineSegment(sketch, "E172", {"start": v(-11.96, 26.79) * mm, "end": v(-13.54, 26.79) * mm});
            skLineSegment(sketch, "E173", {"start": v(-10.35, 25) * mm, "end": v(-9.54, 26.79) * mm});
            skPoint(sketch, "E173.endSnap0", {"position": v(-12.75, 26.79) * mm});
            skLineSegment(sketch, "E174", {"start": v(-7.16, 25) * mm, "end": v(-7.96, 26.79) * mm});
            skLineSegment(sketch, "E175", {"start": v(-7.96, 26.79) * mm, "end": v(-9.54, 26.79) * mm});
            skLineSegment(sketch, "E176", {"start": v(-23.75, 21.59) * mm, "end": v(-5.75, 21.59) * mm});
            skLineSegment(sketch, "E177.MirrorCS", {"start": v(-11.96, 16.39) * mm, "end": v(-13.54, 16.39) * mm});
            skArc(sketch, "E178.MirrorCS", {"start": v(-10.35, 18.17) * mm, "mid": v(-8.75, 20.64) * mm, "end": v(-7.16, 18.17) * mm});
            skLineSegment(sketch, "E179.MirrorCS", {"start": v(-22.35, 18.17) * mm, "end": v(-21.54, 16.39) * mm});
            skLineSegment(sketch, "E180.MirrorCS", {"start": v(-11.16, 18.17) * mm, "end": v(-11.96, 16.39) * mm});
            skLineSegment(sketch, "E181.MirrorCS", {"start": v(-14.35, 18.17) * mm, "end": v(-13.54, 16.39) * mm});
            skArc(sketch, "E182.MirrorCS", {"start": v(-14.35, 18.17) * mm, "mid": v(-12.75, 20.64) * mm, "end": v(-11.16, 18.17) * mm});
            skLineSegment(sketch, "E183.MirrorCS", {"start": v(-15.96, 16.39) * mm, "end": v(-17.54, 16.39) * mm});
            skLineSegment(sketch, "E184.MirrorCS", {"start": v(-19.16, 18.17) * mm, "end": v(-19.96, 16.39) * mm});
            skPoint(sketch, "E185.MirrorP", {"position": v(-12.75, 16.39) * mm});
            skLineSegment(sketch, "E186.MirrorCS", {"start": v(-19.96, 16.39) * mm, "end": v(-21.54, 16.39) * mm});
            skLineSegment(sketch, "E187.MirrorCS", {"start": v(-15.16, 18.17) * mm, "end": v(-15.96, 16.39) * mm});
            skLineSegment(sketch, "E188.MirrorCS", {"start": v(-18.35, 18.17) * mm, "end": v(-17.54, 16.39) * mm});
            skLineSegment(sketch, "E189.MirrorCS", {"start": v(-10.35, 18.17) * mm, "end": v(-9.54, 16.39) * mm});
            skLineSegment(sketch, "E190.MirrorCS", {"start": v(-7.16, 18.17) * mm, "end": v(-7.96, 16.39) * mm});
            skArc(sketch, "E191.MirrorCS", {"start": v(-18.35, 18.17) * mm, "mid": v(-16.75, 20.64) * mm, "end": v(-15.16, 18.17) * mm});
            skArc(sketch, "E192.MirrorCS", {"start": v(-22.35, 18.17) * mm, "mid": v(-20.75, 20.64) * mm, "end": v(-19.16, 18.17) * mm});
            skLineSegment(sketch, "E193.MirrorCS", {"start": v(-7.96, 16.39) * mm, "end": v(-9.54, 16.39) * mm});
            skArc(sketch, "E194", {"start": v(2.4, 24.68) * mm, "mid": v(3.99, 22.21) * mm, "end": v(5.58, 24.68) * mm});
            skArc(sketch, "E195", {"start": v(6.4, 24.68) * mm, "mid": v(7.99, 22.21) * mm, "end": v(9.58, 24.68) * mm});
            skLineSegment(sketch, "E196", {"start": v(2.4, 24.68) * mm, "end": v(3.2, 26.46) * mm});
            skLineSegment(sketch, "E197", {"start": v(5.58, 24.68) * mm, "end": v(4.78, 26.46) * mm});
            skLineSegment(sketch, "E198", {"start": v(6.4, 24.68) * mm, "end": v(7.2, 26.46) * mm});
            skPoint(sketch, "E198.endSnap0", {"position": v(3.99, 26.46) * mm});
            skLineSegment(sketch, "E199", {"start": v(9.58, 24.68) * mm, "end": v(8.78, 26.46) * mm});
            skArc(sketch, "E200.MirrorCS", {"start": v(6.4, 17.84) * mm, "mid": v(7.99, 20.31) * mm, "end": v(9.58, 17.84) * mm});
            skLineSegment(sketch, "E201.MirrorCS", {"start": v(5.58, 17.84) * mm, "end": v(4.78, 16.06) * mm});
            skLineSegment(sketch, "E202.MirrorCS", {"start": v(2.4, 17.84) * mm, "end": v(3.2, 16.06) * mm});
            skArc(sketch, "E203.MirrorCS", {"start": v(2.4, 17.84) * mm, "mid": v(3.99, 20.31) * mm, "end": v(5.58, 17.84) * mm});
            skPoint(sketch, "E204.MirrorP", {"position": v(3.99, 16.06) * mm});
            skLineSegment(sketch, "E205.MirrorCS", {"start": v(6.4, 17.84) * mm, "end": v(7.2, 16.06) * mm});
            skLineSegment(sketch, "E206.MirrorCS", {"start": v(9.58, 17.84) * mm, "end": v(8.78, 16.06) * mm});
            skLineSegment(sketch, "E207.bottom", {"start": v(0.49, 26.46) * mm, "end": v(3.2, 26.46) * mm});
            skLineSegment(sketch, "E207.top", {"start": v(0.49, 16.06) * mm, "end": v(3.2, 16.06) * mm});
            skLineSegment(sketch, "E207.left", {"start": v(0.49, 26.46) * mm, "end": v(0.49, 16.06) * mm});
            skLineSegment(sketch, "E207.right", {"start": v(11.49, 26.46) * mm, "end": v(11.49, 16.06) * mm});
            skLineSegment(sketch, "E208.trimOffspring", {"start": v(8.78, 26.46) * mm, "end": v(11.49, 26.46) * mm});
            skLineSegment(sketch, "E209.trimOffspring", {"start": v(8.78, 16.06) * mm, "end": v(11.49, 16.06) * mm});
            skLineSegment(sketch, "E210.trimOffspring", {"start": v(4.78, 16.06) * mm, "end": v(7.2, 16.06) * mm});
            skLineSegment(sketch, "E211.trimOffspring", {"start": v(4.78, 26.46) * mm, "end": v(7.2, 26.46) * mm});
            skSolve(sketch);
        }
        {
            var Q0;
            Q0 = qSketchRegion(id + "F8", true);
            extrude(context, id + "F9", {"entities" : qUnion([Q0]), "operationType" : NewBodyOperationType.REMOVE, "oppositeDirection" : true, "depth" : 25 * mm});
        }
        {
            var Q0;
            Q0=makeQuery(id+"F9.boolean.opBoolean","COPY",EDGE,{"derivedFrom":makeQuery(id+"F9.opExtrude","SWEPT_EDGE",EDGE,{"disambiguationData":[OSD([sQuery(id+"F6.wireOp",EDGE,"E159.bottom"),sQuery(id+"F8.wireOp",EDGE,"E164"),sQuery(id+"F8.wireOp",EDGE,"E166")])]})});
            var Q1;
            Q1=makeQuery(id+"F9.boolean.opBoolean","COPY",EDGE,{"derivedFrom":makeQuery(id+"F9.opExtrude","SWEPT_EDGE",EDGE,{"disambiguationData":[OSD([sQuery(id+"F6.wireOp",EDGE,"E159.bottom"),sQuery(id+"F8.wireOp",EDGE,"E165"),sQuery(id+"F8.wireOp",EDGE,"E166")])]})});
            var Q2;
            Q2=makeQuery(id+"F9.boolean.opBoolean","COPY",EDGE,{"derivedFrom":makeQuery(id+"F9.opExtrude","SWEPT_EDGE",EDGE,{"disambiguationData":[OSD([sQuery(id+"F6.wireOp",EDGE,"E159.bottom"),sQuery(id+"F8.wireOp",EDGE,"E167"),sQuery(id+"F8.wireOp",EDGE,"E169")])]})});
            var Q3;
            Q3=makeQuery(id+"F9.boolean.opBoolean","COPY",EDGE,{"derivedFrom":makeQuery(id+"F9.opExtrude","SWEPT_EDGE",EDGE,{"disambiguationData":[OSD([sQuery(id+"F6.wireOp",EDGE,"E159.bottom"),sQuery(id+"F8.wireOp",EDGE,"E168"),sQuery(id+"F8.wireOp",EDGE,"E169")])]})});
            var Q4;
            Q4=makeQuery(id+"F9.boolean.opBoolean","COPY",EDGE,{"derivedFrom":makeQuery(id+"F9.opExtrude","SWEPT_EDGE",EDGE,{"disambiguationData":[OSD([sQuery(id+"F6.wireOp",EDGE,"E159.bottom"),sQuery(id+"F8.wireOp",EDGE,"E170"),sQuery(id+"F8.wireOp",EDGE,"E172")])]})});
            var Q5;
            Q5=makeQuery(id+"F9.boolean.opBoolean","COPY",EDGE,{"derivedFrom":makeQuery(id+"F9.opExtrude","SWEPT_EDGE",EDGE,{"disambiguationData":[OSD([sQuery(id+"F6.wireOp",EDGE,"E159.bottom"),sQuery(id+"F8.wireOp",EDGE,"E171"),sQuery(id+"F8.wireOp",EDGE,"E172")])]})});
            var Q6;
            Q6=makeQuery(id+"F9.boolean.opBoolean","COPY",EDGE,{"derivedFrom":makeQuery(id+"F9.opExtrude","SWEPT_EDGE",EDGE,{"disambiguationData":[OSD([sQuery(id+"F6.wireOp",EDGE,"E159.bottom"),sQuery(id+"F8.wireOp",EDGE,"E173"),sQuery(id+"F8.wireOp",EDGE,"E175")])]})});
            var Q7;
            Q7=makeQuery(id+"F9.boolean.opBoolean","COPY",EDGE,{"derivedFrom":makeQuery(id+"F9.opExtrude","SWEPT_EDGE",EDGE,{"disambiguationData":[OSD([sQuery(id+"F6.wireOp",EDGE,"E159.bottom"),sQuery(id+"F8.wireOp",EDGE,"E174"),sQuery(id+"F8.wireOp",EDGE,"E175")])]})});
            var Q8;
            Q8=makeQuery(id+"F9.boolean.opBoolean","COPY",EDGE,{"derivedFrom":makeQuery(id+"F9.opExtrude","SWEPT_EDGE",EDGE,{"disambiguationData":[OSD([sQuery(id+"F6.wireOp",EDGE,"E159.top"),sQuery(id+"F8.wireOp",EDGE,"E179.MirrorCS"),sQuery(id+"F8.wireOp",EDGE,"E186.MirrorCS")])]})});
            var Q9;
            Q9=makeQuery(id+"F9.boolean.opBoolean","COPY",EDGE,{"derivedFrom":makeQuery(id+"F9.opExtrude","SWEPT_EDGE",EDGE,{"disambiguationData":[OSD([sQuery(id+"F6.wireOp",EDGE,"E159.top"),sQuery(id+"F8.wireOp",EDGE,"E183.MirrorCS"),sQuery(id+"F8.wireOp",EDGE,"E188.MirrorCS")])]})});
            var Q10;
            Q10=makeQuery(id+"F9.boolean.opBoolean","COPY",EDGE,{"derivedFrom":makeQuery(id+"F9.opExtrude","SWEPT_EDGE",EDGE,{"disambiguationData":[OSD([sQuery(id+"F6.wireOp",EDGE,"E159.top"),sQuery(id+"F8.wireOp",EDGE,"E184.MirrorCS"),sQuery(id+"F8.wireOp",EDGE,"E186.MirrorCS")])]})});
            var Q11;
            Q11=makeQuery(id+"F9.boolean.opBoolean","COPY",EDGE,{"derivedFrom":makeQuery(id+"F9.opExtrude","SWEPT_EDGE",EDGE,{"disambiguationData":[OSD([sQuery(id+"F6.wireOp",EDGE,"E159.top"),sQuery(id+"F8.wireOp",EDGE,"E183.MirrorCS"),sQuery(id+"F8.wireOp",EDGE,"E187.MirrorCS")])]})});
            var Q12;
            Q12=makeQuery(id+"F9.boolean.opBoolean","COPY",EDGE,{"derivedFrom":makeQuery(id+"F9.opExtrude","SWEPT_EDGE",EDGE,{"disambiguationData":[OSD([sQuery(id+"F6.wireOp",EDGE,"E159.top"),sQuery(id+"F8.wireOp",EDGE,"E177.MirrorCS"),sQuery(id+"F8.wireOp",EDGE,"E181.MirrorCS")])]})});
            var Q13;
            Q13=makeQuery(id+"F9.boolean.opBoolean","COPY",EDGE,{"derivedFrom":makeQuery(id+"F9.opExtrude","SWEPT_EDGE",EDGE,{"disambiguationData":[OSD([sQuery(id+"F6.wireOp",EDGE,"E159.top"),sQuery(id+"F8.wireOp",EDGE,"E177.MirrorCS"),sQuery(id+"F8.wireOp",EDGE,"E180.MirrorCS")])]})});
            var Q14;
            Q14=makeQuery(id+"F9.boolean.opBoolean","COPY",EDGE,{"derivedFrom":makeQuery(id+"F9.opExtrude","SWEPT_EDGE",EDGE,{"disambiguationData":[OSD([sQuery(id+"F6.wireOp",EDGE,"E159.top"),sQuery(id+"F8.wireOp",EDGE,"E189.MirrorCS"),sQuery(id+"F8.wireOp",EDGE,"E193.MirrorCS")])]})});
            var Q15;
            Q15=makeQuery(id+"F9.boolean.opBoolean","COPY",EDGE,{"derivedFrom":makeQuery(id+"F9.opExtrude","SWEPT_EDGE",EDGE,{"disambiguationData":[OSD([sQuery(id+"F6.wireOp",EDGE,"E159.top"),sQuery(id+"F8.wireOp",EDGE,"E190.MirrorCS"),sQuery(id+"F8.wireOp",EDGE,"E193.MirrorCS")])]})});
            fillet(context, id + "F10", {"entities" : qUnion([Q0, Q1, Q2, Q3, Q4, Q5, Q6, Q7, Q8, Q9, Q10, Q11, Q12, Q13, Q14, Q15]), "radius" : .75 * mm, "tangentPropagation" : true, "allowEdgeOverflow" : false});
        }
        {
            var Q0;
            Q0=makeQuery(id+"F7.opExtrude","SWEPT_EDGE",EDGE,{"disambiguationData":[OSD([sQuery(id+"F6.wireOp",EDGE,"E159.top"),sQuery(id+"F6.wireOp",EDGE,"E159.right")])]});
            var Q1;
            Q1=makeQuery(id+"F7.opExtrude","SWEPT_EDGE",EDGE,{"disambiguationData":[OSD([sQuery(id+"F6.wireOp",EDGE,"E159.top"),sQuery(id+"F6.wireOp",EDGE,"E159.left")])]});
            var Q2;
            Q2=makeQuery(id+"F7.opExtrude","SWEPT_EDGE",EDGE,{"disambiguationData":[OSD([sQuery(id+"F6.wireOp",EDGE,"E159.bottom"),sQuery(id+"F6.wireOp",EDGE,"E159.right")])]});
            var Q3;
            Q3=makeQuery(id+"F7.opExtrude","SWEPT_EDGE",EDGE,{"disambiguationData":[OSD([sQuery(id+"F6.wireOp",EDGE,"E159.bottom"),sQuery(id+"F6.wireOp",EDGE,"E159.left")])]});
            fillet(context, id + "F11", {"entities" : qUnion([Q0, Q1, Q2, Q3]), "radius" : 4 * mm, "tangentPropagation" : true, "allowEdgeOverflow" : false});
        }
        {
            var Q0;
            Q0=qCreatedBy(makeId("Top.planeOp"),FACE);
            var sketch = newSketch(context, id + "F12", { "sketchPlane" : qUnion([Q0])});
            skArc(sketch, "E212", {"start": v(-24.05, -7.66) * mm, "mid": v(-22.46, -10.13) * mm, "end": v(-20.86, -7.66) * mm});
            skArc(sketch, "E213", {"start": v(-20.05, -7.66) * mm, "mid": v(-18.46, -10.13) * mm, "end": v(-16.86, -7.66) * mm});
            skLineSegment(sketch, "E214", {"start": v(-24.05, -7.66) * mm, "end": v(-23.25, -5.88) * mm});
            skLineSegment(sketch, "E215", {"start": v(-20.86, -7.66) * mm, "end": v(-21.67, -5.88) * mm});
            skLineSegment(sketch, "E216", {"start": v(-20.05, -7.66) * mm, "end": v(-19.25, -5.88) * mm});
            skPoint(sketch, "E216.endSnap0", {"position": v(-22.46, -5.88) * mm});
            skLineSegment(sketch, "E217", {"start": v(-16.86, -7.66) * mm, "end": v(-17.67, -5.88) * mm});
            skArc(sketch, "E218.MirrorCS", {"start": v(-20.05, -14.5) * mm, "mid": v(-18.46, -12.03) * mm, "end": v(-16.86, -14.5) * mm});
            skLineSegment(sketch, "E219.MirrorCS", {"start": v(-20.86, -14.5) * mm, "end": v(-21.67, -16.28) * mm});
            skLineSegment(sketch, "E220.MirrorCS", {"start": v(-24.05, -14.5) * mm, "end": v(-23.25, -16.28) * mm});
            skArc(sketch, "E221.MirrorCS", {"start": v(-24.05, -14.5) * mm, "mid": v(-22.46, -12.03) * mm, "end": v(-20.86, -14.5) * mm});
            skPoint(sketch, "E222.MirrorP", {"position": v(-22.46, -16.28) * mm});
            skLineSegment(sketch, "E223.MirrorCS", {"start": v(-20.05, -14.5) * mm, "end": v(-19.25, -16.28) * mm});
            skLineSegment(sketch, "E224.MirrorCS", {"start": v(-16.86, -14.5) * mm, "end": v(-17.67, -16.28) * mm});
            skLineSegment(sketch, "E225.bottom", {"start": v(-25.96, -5.88) * mm, "end": v(-23.25, -5.88) * mm});
            skLineSegment(sketch, "E225.top", {"start": v(-25.96, -16.28) * mm, "end": v(-23.25, -16.28) * mm});
            skLineSegment(sketch, "E225.left", {"start": v(-25.96, -5.88) * mm, "end": v(-25.96, -16.28) * mm});
            skLineSegment(sketch, "E225.right", {"start": v(-14.96, -5.88) * mm, "end": v(-14.96, -16.28) * mm});
            skLineSegment(sketch, "E226.trimOffspring", {"start": v(-17.67, -5.88) * mm, "end": v(-14.96, -5.88) * mm});
            skLineSegment(sketch, "E227.trimOffspring", {"start": v(-17.67, -16.28) * mm, "end": v(-14.96, -16.28) * mm});
            skLineSegment(sketch, "E228.trimOffspring", {"start": v(-21.67, -16.28) * mm, "end": v(-19.25, -16.28) * mm});
            skLineSegment(sketch, "E229.trimOffspring", {"start": v(-21.67, -5.88) * mm, "end": v(-19.25, -5.88) * mm});
            skSolve(sketch);
        }
        {
            var Q0;
            Q0=makeQuery(id+"F12.imprint","IMPRINT",FACE,{"disambiguationData":[TD([[makeQuery(id+"F12.imprint","IMPRINT",EDGE,{"derivedFrom":sQuery(id+"F12.wireOp",EDGE,"E212")}),-1.0]])]});
            var Q1;
            Q1=makeQuery(id+"F1.opExtrude","CAP_FACE",FACE,{"disambiguationData":[OSD([sQuery(id+"F0.wireOp",EDGE,"E0.bottom"),sQuery(id+"F0.wireOp",EDGE,"E0.top"),sQuery(id+"F0.wireOp",EDGE,"E0.left"),sQuery(id+"F0.wireOp",EDGE,"E0.right")])],"isStart":false});
            extrude(context, id + "F13", {"entities" : qUnion([Q0]), "endBound" : BoundingType.UP_TO_SURFACE, "endBoundEntityFace" : qUnion([Q1]), "depth" : 25 * mm});
        }
        {
            var Q0;
            Q0=makeQuery(id+"F13.opExtrude","SWEPT_EDGE",EDGE,{"disambiguationData":[OSD([sQuery(id+"F12.wireOp",EDGE,"E225.bottom"),sQuery(id+"F12.wireOp",EDGE,"E225.left")])]});
            var Q1;
            Q1=makeQuery(id+"F13.opExtrude","SWEPT_EDGE",EDGE,{"disambiguationData":[OSD([sQuery(id+"F12.wireOp",EDGE,"E225.top"),sQuery(id+"F12.wireOp",EDGE,"E225.left")])]});
            var Q2;
            Q2=makeQuery(id+"F13.opExtrude","SWEPT_EDGE",EDGE,{"disambiguationData":[OSD([sQuery(id+"F12.wireOp",EDGE,"E225.right"),sQuery(id+"F12.wireOp",EDGE,"E227.trimOffspring")])]});
            var Q3;
            Q3=makeQuery(id+"F13.opExtrude","SWEPT_EDGE",EDGE,{"disambiguationData":[OSD([sQuery(id+"F12.wireOp",EDGE,"E225.right"),sQuery(id+"F12.wireOp",EDGE,"E226.trimOffspring")])]});
            fillet(context, id + "F14", {"entities" : qUnion([Q0, Q1, Q2, Q3]), "radius" : 2 * mm, "tangentPropagation" : true, "allowEdgeOverflow" : false});
        }
        {
            var Q0;
            Q0=makeQuery(id+"F13.opExtrude","SWEPT_EDGE",EDGE,{"disambiguationData":[OSD([sQuery(id+"F12.wireOp",EDGE,"E220.MirrorCS"),sQuery(id+"F12.wireOp",EDGE,"E225.top")])]});
            var Q1;
            Q1=makeQuery(id+"F13.opExtrude","SWEPT_EDGE",EDGE,{"disambiguationData":[OSD([sQuery(id+"F12.wireOp",EDGE,"E219.MirrorCS"),sQuery(id+"F12.wireOp",EDGE,"E228.trimOffspring")])]});
            var Q2;
            Q2=makeQuery(id+"F13.opExtrude","SWEPT_EDGE",EDGE,{"disambiguationData":[OSD([sQuery(id+"F12.wireOp",EDGE,"E223.MirrorCS"),sQuery(id+"F12.wireOp",EDGE,"E228.trimOffspring")])]});
            var Q3;
            Q3=makeQuery(id+"F13.opExtrude","SWEPT_EDGE",EDGE,{"disambiguationData":[OSD([sQuery(id+"F12.wireOp",EDGE,"E224.MirrorCS"),sQuery(id+"F12.wireOp",EDGE,"E227.trimOffspring")])]});
            var Q4;
            Q4=makeQuery(id+"F13.opExtrude","SWEPT_EDGE",EDGE,{"disambiguationData":[OSD([sQuery(id+"F12.wireOp",EDGE,"E217"),sQuery(id+"F12.wireOp",EDGE,"E226.trimOffspring")])]});
            var Q5;
            Q5=makeQuery(id+"F13.opExtrude","SWEPT_EDGE",EDGE,{"disambiguationData":[OSD([sQuery(id+"F12.wireOp",EDGE,"E216"),sQuery(id+"F12.wireOp",EDGE,"E229.trimOffspring")])]});
            var Q6;
            Q6=makeQuery(id+"F13.opExtrude","SWEPT_EDGE",EDGE,{"disambiguationData":[OSD([sQuery(id+"F12.wireOp",EDGE,"E215"),sQuery(id+"F12.wireOp",EDGE,"E229.trimOffspring")])]});
            var Q7;
            Q7=makeQuery(id+"F13.opExtrude","SWEPT_EDGE",EDGE,{"disambiguationData":[OSD([sQuery(id+"F12.wireOp",EDGE,"E214"),sQuery(id+"F12.wireOp",EDGE,"E225.bottom")])]});
            fillet(context, id + "F15", {"entities" : qUnion([Q0, Q1, Q2, Q3, Q4, Q5, Q6, Q7]), "radius" : .75 * mm, "tangentPropagation" : true, "allowEdgeOverflow" : false});
        }
        {
            var Q0;
            Q0=makeQuery(id+"F2.imprint","IMPRINT",FACE,{"disambiguationData":[TD([[makeQuery(id+"F2.imprint","IMPRINT",EDGE,{"derivedFrom":sQuery(id+"F2.wireOp",EDGE,"E99")}),-1.0]])]});
            extrude(context, id + "F16", {"entities" : qUnion([Q0]), "oppositeDirection" : true, "depth" : 2.75 * mm});
        }
        {
            var Q0;
            Q0=makeQuery(id+"F16.opExtrude","SWEPT_EDGE",EDGE,{"disambiguationData":[OSD([sQuery(id+"F2.wireOp",EDGE,"E123.bottom"),sQuery(id+"F2.wireOp",EDGE,"E123.left")])]});
            var Q1;
            Q1=makeQuery(id+"F16.opExtrude","SWEPT_EDGE",EDGE,{"disambiguationData":[OSD([sQuery(id+"F2.wireOp",EDGE,"E156"),sQuery(id+"F2.wireOp",EDGE,"E158")])]});
            var Q2;
            Q2=makeQuery(id+"F16.opExtrude","SWEPT_EDGE",EDGE,{"disambiguationData":[OSD([sQuery(id+"F2.wireOp",EDGE,"E156"),sQuery(id+"F2.wireOp",EDGE,"E157")])]});
            var Q3;
            Q3=makeQuery(id+"F16.opExtrude","SWEPT_EDGE",EDGE,{"disambiguationData":[OSD([sQuery(id+"F2.wireOp",EDGE,"E123.top"),sQuery(id+"F2.wireOp",EDGE,"E123.left")])]});
            fillet(context, id + "F17", {"entities" : qUnion([Q0, Q1, Q2, Q3]), "radius" : 2 * mm, "tangentPropagation" : true, "allowEdgeOverflow" : false});
        }
        {
            var Q0;
            Q0=makeQuery(id+"F16.opExtrude","SWEPT_EDGE",EDGE,{"disambiguationData":[OSD([sQuery(id+"F2.wireOp",EDGE,"E103"),sQuery(id+"F2.wireOp",EDGE,"E123.bottom")])]});
            var Q1;
            Q1=makeQuery(id+"F16.opExtrude","SWEPT_EDGE",EDGE,{"disambiguationData":[OSD([sQuery(id+"F2.wireOp",EDGE,"E100"),sQuery(id+"F2.wireOp",EDGE,"E129.trimOffspring")])]});
            var Q2;
            Q2=makeQuery(id+"F16.opExtrude","SWEPT_EDGE",EDGE,{"disambiguationData":[OSD([sQuery(id+"F2.wireOp",EDGE,"E122.MirrorCS"),sQuery(id+"F2.wireOp",EDGE,"E129.trimOffspring")])]});
            var Q3;
            Q3=makeQuery(id+"F16.opExtrude","SWEPT_EDGE",EDGE,{"disambiguationData":[OSD([sQuery(id+"F2.wireOp",EDGE,"E119.MirrorCS"),sQuery(id+"F2.wireOp",EDGE,"E128.trimOffspring")])]});
            var Q4;
            Q4=makeQuery(id+"F16.opExtrude","SWEPT_EDGE",EDGE,{"disambiguationData":[OSD([sQuery(id+"F2.wireOp",EDGE,"E120.MirrorCS"),sQuery(id+"F2.wireOp",EDGE,"E128.trimOffspring")])]});
            var Q5;
            Q5=makeQuery(id+"F16.opExtrude","SWEPT_EDGE",EDGE,{"disambiguationData":[OSD([sQuery(id+"F2.wireOp",EDGE,"E115.MirrorCS"),sQuery(id+"F2.wireOp",EDGE,"E127.trimOffspring")])]});
            var Q6;
            Q6=makeQuery(id+"F16.opExtrude","SWEPT_EDGE",EDGE,{"disambiguationData":[OSD([sQuery(id+"F2.wireOp",EDGE,"E114.MirrorCS"),sQuery(id+"F2.wireOp",EDGE,"E127.trimOffspring")])]});
            var Q7;
            Q7=makeQuery(id+"F16.opExtrude","SWEPT_EDGE",EDGE,{"disambiguationData":[OSD([sQuery(id+"F2.wireOp",EDGE,"E118.MirrorCS"),sQuery(id+"F2.wireOp",EDGE,"E130")])]});
            var Q8;
            Q8=makeQuery(id+"F16.opExtrude","SWEPT_EDGE",EDGE,{"disambiguationData":[OSD([sQuery(id+"F2.wireOp",EDGE,"E145.MirrorCS"),sQuery(id+"F2.wireOp",EDGE,"E154")])]});
            var Q9;
            Q9=makeQuery(id+"F16.opExtrude","SWEPT_EDGE",EDGE,{"disambiguationData":[OSD([sQuery(id+"F2.wireOp",EDGE,"E133.MirrorCS"),sQuery(id+"F2.wireOp",EDGE,"E137.MirrorCS")])]});
            var Q10;
            Q10=makeQuery(id+"F16.opExtrude","SWEPT_EDGE",EDGE,{"disambiguationData":[OSD([sQuery(id+"F2.wireOp",EDGE,"E135.MirrorCS"),sQuery(id+"F2.wireOp",EDGE,"E137.MirrorCS")])]});
            var Q11;
            Q11=makeQuery(id+"F16.opExtrude","SWEPT_EDGE",EDGE,{"disambiguationData":[OSD([sQuery(id+"F2.wireOp",EDGE,"E132.MirrorCS"),sQuery(id+"F2.wireOp",EDGE,"E150.MirrorCS")])]});
            var Q12;
            Q12=makeQuery(id+"F16.opExtrude","SWEPT_EDGE",EDGE,{"disambiguationData":[OSD([sQuery(id+"F2.wireOp",EDGE,"E132.MirrorCS"),sQuery(id+"F2.wireOp",EDGE,"E151.MirrorCS")])]});
            var Q13;
            Q13=makeQuery(id+"F16.opExtrude","SWEPT_EDGE",EDGE,{"disambiguationData":[OSD([sQuery(id+"F2.wireOp",EDGE,"E142.MirrorCS"),sQuery(id+"F2.wireOp",EDGE,"E158")])]});
            var Q14;
            Q14=makeQuery(id+"F16.opExtrude","SWEPT_EDGE",EDGE,{"disambiguationData":[OSD([sQuery(id+"F2.wireOp",EDGE,"E147.MirrorCS"),sQuery(id+"F2.wireOp",EDGE,"E157")])]});
            var Q15;
            Q15=makeQuery(id+"F16.opExtrude","SWEPT_EDGE",EDGE,{"disambiguationData":[OSD([sQuery(id+"F2.wireOp",EDGE,"E136.MirrorCS"),sQuery(id+"F2.wireOp",EDGE,"E153.MirrorCS")])]});
            var Q16;
            Q16=makeQuery(id+"F16.opExtrude","SWEPT_EDGE",EDGE,{"disambiguationData":[OSD([sQuery(id+"F2.wireOp",EDGE,"E136.MirrorCS"),sQuery(id+"F2.wireOp",EDGE,"E143.MirrorCS")])]});
            var Q17;
            Q17=makeQuery(id+"F16.opExtrude","SWEPT_EDGE",EDGE,{"disambiguationData":[OSD([sQuery(id+"F2.wireOp",EDGE,"E134.MirrorCS"),sQuery(id+"F2.wireOp",EDGE,"E146.MirrorCS")])]});
            var Q18;
            Q18=makeQuery(id+"F16.opExtrude","SWEPT_EDGE",EDGE,{"disambiguationData":[OSD([sQuery(id+"F2.wireOp",EDGE,"E144.MirrorCS"),sQuery(id+"F2.wireOp",EDGE,"E146.MirrorCS")])]});
            var Q19;
            Q19=makeQuery(id+"F16.opExtrude","SWEPT_EDGE",EDGE,{"disambiguationData":[OSD([sQuery(id+"F2.wireOp",EDGE,"E152.MirrorCS"),sQuery(id+"F2.wireOp",EDGE,"E155")])]});
            var Q20;
            Q20=makeQuery(id+"F16.opExtrude","SWEPT_EDGE",EDGE,{"disambiguationData":[OSD([sQuery(id+"F2.wireOp",EDGE,"E117.MirrorCS"),sQuery(id+"F2.wireOp",EDGE,"E131")])]});
            var Q21;
            Q21=makeQuery(id+"F16.opExtrude","SWEPT_EDGE",EDGE,{"disambiguationData":[OSD([sQuery(id+"F2.wireOp",EDGE,"E121.MirrorCS"),sQuery(id+"F2.wireOp",EDGE,"E126.trimOffspring")])]});
            var Q22;
            Q22=makeQuery(id+"F16.opExtrude","SWEPT_EDGE",EDGE,{"disambiguationData":[OSD([sQuery(id+"F2.wireOp",EDGE,"E110.MirrorCS"),sQuery(id+"F2.wireOp",EDGE,"E126.trimOffspring")])]});
            var Q23;
            Q23=makeQuery(id+"F16.opExtrude","SWEPT_EDGE",EDGE,{"disambiguationData":[OSD([sQuery(id+"F2.wireOp",EDGE,"E106.MirrorCS"),sQuery(id+"F2.wireOp",EDGE,"E125.trimOffspring")])]});
            var Q24;
            Q24=makeQuery(id+"F16.opExtrude","SWEPT_EDGE",EDGE,{"disambiguationData":[OSD([sQuery(id+"F2.wireOp",EDGE,"E111.MirrorCS"),sQuery(id+"F2.wireOp",EDGE,"E125.trimOffspring")])]});
            var Q25;
            Q25=makeQuery(id+"F16.opExtrude","SWEPT_EDGE",EDGE,{"disambiguationData":[OSD([sQuery(id+"F2.wireOp",EDGE,"E116.MirrorCS"),sQuery(id+"F2.wireOp",EDGE,"E124.trimOffspring")])]});
            var Q26;
            Q26=makeQuery(id+"F16.opExtrude","SWEPT_EDGE",EDGE,{"disambiguationData":[OSD([sQuery(id+"F2.wireOp",EDGE,"E102.MirrorCS"),sQuery(id+"F2.wireOp",EDGE,"E124.trimOffspring")])]});
            var Q27;
            Q27=makeQuery(id+"F16.opExtrude","SWEPT_EDGE",EDGE,{"disambiguationData":[OSD([sQuery(id+"F2.wireOp",EDGE,"E104"),sQuery(id+"F2.wireOp",EDGE,"E123.top")])]});
            fillet(context, id + "F18", {"entities" : qUnion([Q0, Q1, Q2, Q3, Q4, Q5, Q6, Q7, Q8, Q9, Q10, Q11, Q12, Q13, Q14, Q15, Q16, Q17, Q18, Q19, Q20, Q21, Q22, Q23, Q24, Q25, Q26, Q27]), "radius" : .75 * mm, "tangentPropagation" : true, "allowEdgeOverflow" : false});
        }
    });
